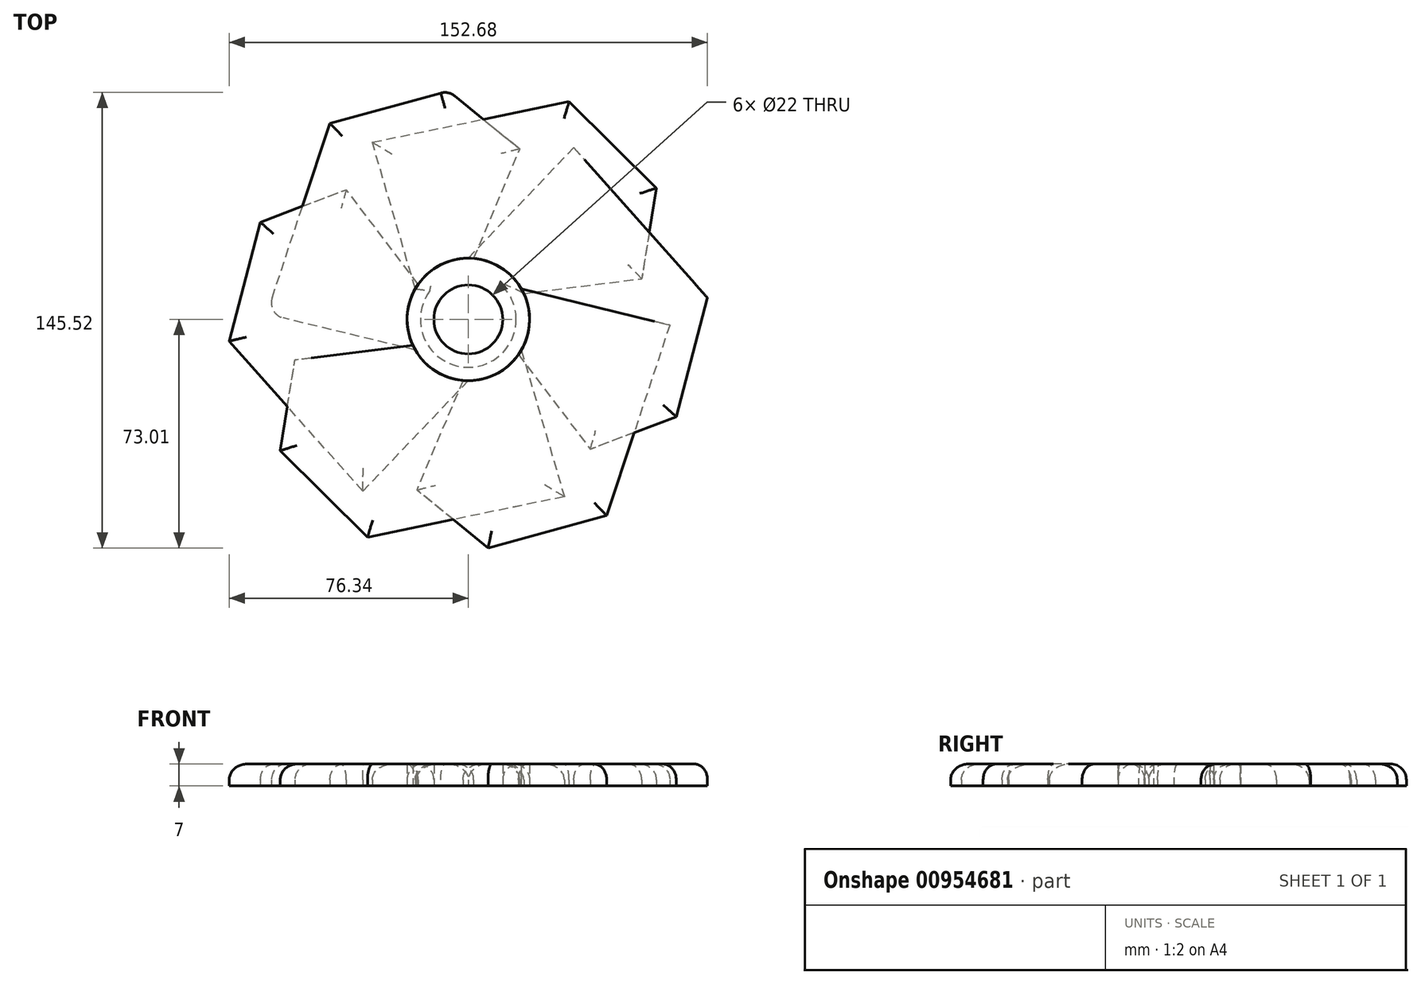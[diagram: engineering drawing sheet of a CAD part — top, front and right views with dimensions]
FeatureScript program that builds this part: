
annotation { "Feature Type Name" : "Feature", "Feature Type Description" : "" }
export const myFeature = defineFeature(function(context is Context, id is Id, definition is map)
    precondition{}
    {
        {
            var Q0;
            Q0=qCreatedBy(makeId("Top.planeOp"),FACE);
            var sketch = newSketch(context, id + "F0", { "sketchPlane" : qUnion([Q0])});
            skArc(sketch, "E0", {"start": v(0, 11) * mm, "mid": v(-7.37, -8.17) * mm, "end": v(10.94, 1.14) * mm});
            skCircle(sketch, "E1", {"center": v(0, 0) * mm, "radius": 11 * mm});
            skArc(sketch, "E2", {"start": v(0, 19.55) * mm, "mid": v(-17.34, -9.03) * mm, "end": v(16.02, -11.21) * mm});
            skArc(sketch, "E3", {"start": v(56.29, -3.64) * mm, "mid": v(30.94, 14.76) * mm, "end": v(0, 19.55) * mm});
            skArc(sketch, "E4", {"start": v(54.87, -7) * mm, "mid": v(34.86, -3.73) * mm, "end": v(16.02, -11.21) * mm});
            skLineSegment(sketch, "E5", {"start": v(56.29, -3.64) * mm, "end": v(56.29, -6.1) * mm});
            skPoint(sketch, "E6.orphan", {"position": v(61.87, -11.21) * mm});
            skPoint(sketch, "E7.visualSharp", {"position": v(56.29, -7.7) * mm});
            skArc(sketch, "E7.filletArc", {"start": v(54.87, -7) * mm, "mid": v(55.82, -6.94) * mm, "end": v(56.29, -6.1) * mm});
            skLineSegment(sketch, "E8", {"start": v(16.02, -11.21) * mm, "end": v(38.94, -41.46) * mm});
            skLineSegment(sketch, "E9", {"start": v(56.29, -7.7) * mm, "end": v(38.94, -41.46) * mm});
            skLineSegment(sketch, "E10", {"start": v(0, 19.55) * mm, "end": v(33.7, 54.86) * mm});
            skLineSegment(sketch, "E11", {"start": v(33.7, 54.86) * mm, "end": v(56.29, -3.64) * mm});
            skLineSegment(sketch, "E12", {"start": v(33.7, 54.86) * mm, "end": v(76.34, 6.93) * mm});
            skLineSegment(sketch, "E13", {"start": v(76.34, 6.93) * mm, "end": v(66.38, -31.05) * mm});
            skLineSegment(sketch, "E14", {"start": v(66.38, -31.05) * mm, "end": v(38.94, -41.46) * mm});
            skSolve(sketch);
        }
        {
            var Q0;
            Q0 = qSketchRegion(id + "F0", true);
            extrude(context, id + "F1", {"entities" : qUnion([Q0]), "endBound" : BoundingType.SYMMETRIC, "depth" : 7 * mm, "offsetDistance" : 25 * mm});
        }
        {
            var Q0;
            Q0=makeQuery(id+"F1.opExtrude","SWEPT_BODY",BODY,{"disambiguationData":[OSD([sQuery(id+"F0.wireOp",EDGE,"E1"),sQuery(id+"F0.wireOp",EDGE,"E2"),sQuery(id+"F0.wireOp",EDGE,"E3"),sQuery(id+"F0.wireOp",EDGE,"E4")])]});
            var Q1;
            Q1=makeQuery(id+"F1.opExtrude","CAP_EDGE",EDGE,{"disambiguationData":[OSD([sQuery(id+"F0.wireOp",EDGE,"E1")])],"isStart":false});
            circularPattern(context, id + "F2", {"entities" : qUnion([Q0]), "axis" : qUnion([Q1]), "angle" : 360 * degree, "instanceCount" : 6, "equalSpace" : true});
        }
        {
            var Q0;
            Q0=makeQuery(id+"F2.opPattern","COPY",EDGE,{"derivedFrom":makeQuery(id+"F1.opExtrude","CAP_EDGE",EDGE,{"disambiguationData":[OSD([sQuery(id+"F0.wireOp",EDGE,"E13")])],"isStart":false}),"instanceName":"2"});
            var Q1;
            Q1=makeQuery(id+"F2.opPattern","COPY",EDGE,{"derivedFrom":makeQuery(id+"F1.opExtrude","CAP_EDGE",EDGE,{"disambiguationData":[OSD([sQuery(id+"F0.wireOp",EDGE,"E12")])],"isStart":false}),"instanceName":"2"});
            fillet(context, id + "F3", {"entities" : qUnion([Q0, Q1]), "tangentPropagation" : true, "radius" : 5 * mm, "defaultsChanged" : false, "vertexSettings" : [], "allowEdgeOverflow" : false});
        }
        {
            var Q0;
            Q0=makeQuery(id+"F2.opPattern","COPY",EDGE,{"derivedFrom":makeQuery(id+"F1.opExtrude","CAP_EDGE",EDGE,{"disambiguationData":[OSD([sQuery(id+"F0.wireOp",EDGE,"E14")])],"isStart":false}),"instanceName":"3"});
            var Q1;
            Q1=makeQuery(id+"F2.opPattern","COPY",EDGE,{"derivedFrom":makeQuery(id+"F1.opExtrude","CAP_EDGE",EDGE,{"disambiguationData":[OSD([sQuery(id+"F0.wireOp",EDGE,"E13")])],"isStart":false}),"instanceName":"3"});
            var Q2;
            Q2=makeQuery(id+"F2.opPattern","COPY",EDGE,{"derivedFrom":makeQuery(id+"F1.opExtrude","CAP_EDGE",EDGE,{"disambiguationData":[OSD([sQuery(id+"F0.wireOp",EDGE,"E12")])],"isStart":false}),"instanceName":"3"});
            var Q3;
            Q3=makeQuery(id+"F2.opPattern","COPY",EDGE,{"derivedFrom":makeQuery(id+"F1.opExtrude","CAP_EDGE",EDGE,{"disambiguationData":[OSD([sQuery(id+"F0.wireOp",EDGE,"E14")])],"isStart":false}),"instanceName":"4"});
            var Q4;
            Q4=makeQuery(id+"F2.opPattern","COPY",EDGE,{"derivedFrom":makeQuery(id+"F1.opExtrude","CAP_EDGE",EDGE,{"disambiguationData":[OSD([sQuery(id+"F0.wireOp",EDGE,"E13")])],"isStart":false}),"instanceName":"4"});
            var Q5;
            Q5=makeQuery(id+"F2.opPattern","COPY",EDGE,{"derivedFrom":makeQuery(id+"F1.opExtrude","CAP_EDGE",EDGE,{"disambiguationData":[OSD([sQuery(id+"F0.wireOp",EDGE,"E12")])],"isStart":false}),"instanceName":"4"});
            var Q6;
            Q6=makeQuery(id+"F2.opPattern","COPY",EDGE,{"derivedFrom":makeQuery(id+"F1.opExtrude","CAP_EDGE",EDGE,{"disambiguationData":[OSD([sQuery(id+"F0.wireOp",EDGE,"E14")])],"isStart":false}),"instanceName":"5"});
            var Q7;
            Q7=makeQuery(id+"F2.opPattern","COPY",EDGE,{"derivedFrom":makeQuery(id+"F1.opExtrude","CAP_EDGE",EDGE,{"disambiguationData":[OSD([sQuery(id+"F0.wireOp",EDGE,"E13")])],"isStart":false}),"instanceName":"5"});
            var Q8;
            Q8=makeQuery(id+"F2.opPattern","COPY",EDGE,{"derivedFrom":makeQuery(id+"F1.opExtrude","CAP_EDGE",EDGE,{"disambiguationData":[OSD([sQuery(id+"F0.wireOp",EDGE,"E12")])],"isStart":false}),"instanceName":"5"});
            var Q9;
            Q9=makeQuery(id+"F1.opExtrude","CAP_EDGE",EDGE,{"disambiguationData":[OSD([sQuery(id+"F0.wireOp",EDGE,"E14")])],"isStart":false});
            var Q10;
            Q10=makeQuery(id+"F1.opExtrude","CAP_EDGE",EDGE,{"disambiguationData":[OSD([sQuery(id+"F0.wireOp",EDGE,"E8")])],"isStart":false});
            var Q11;
            Q11=makeQuery(id+"F2.opPattern","COPY",EDGE,{"derivedFrom":makeQuery(id+"F1.opExtrude","CAP_EDGE",EDGE,{"disambiguationData":[OSD([sQuery(id+"F0.wireOp",EDGE,"E10")])],"isStart":false}),"instanceName":"4"});
            var Q12;
            Q12=makeQuery(id+"F2.opPattern","COPY",EDGE,{"derivedFrom":makeQuery(id+"F1.opExtrude","CAP_EDGE",EDGE,{"disambiguationData":[OSD([sQuery(id+"F0.wireOp",EDGE,"E8")])],"isStart":false}),"instanceName":"5"});
            var Q13;
            Q13=makeQuery(id+"F2.opPattern","COPY",EDGE,{"derivedFrom":makeQuery(id+"F1.opExtrude","CAP_EDGE",EDGE,{"disambiguationData":[OSD([sQuery(id+"F0.wireOp",EDGE,"E10")])],"isStart":false}),"instanceName":"3"});
            var Q14;
            Q14=makeQuery(id+"F2.opPattern","COPY",EDGE,{"derivedFrom":makeQuery(id+"F1.opExtrude","CAP_EDGE",EDGE,{"disambiguationData":[OSD([sQuery(id+"F0.wireOp",EDGE,"E10")])],"isStart":false}),"instanceName":"2"});
            var Q15;
            {var subQ0=sQuery(id+"F0.wireOp",EDGE,"E12");Q15=makeQuery(id+"F3.opFillet","BLEND_EDGE",EDGE,{"blendedFrom":[makeQuery(id+"F2.opPattern","COPY",EDGE,{"derivedFrom":makeQuery(id+"F1.opExtrude","CAP_EDGE",EDGE,{"disambiguationData":[OSD([subQ0])],"isStart":false}),"instanceName":"2"}),makeQuery(id+"F2.opPattern","COPY",FACE,{"derivedFrom":makeQuery(id+"F1.opExtrude","CAP_FACE",FACE,{"disambiguationData":[OSD([sQuery(id+"F0.wireOp",EDGE,"E1"),sQuery(id+"F0.wireOp",EDGE,"E2"),sQuery(id+"F0.wireOp",EDGE,"E8"),sQuery(id+"F0.wireOp",EDGE,"E10"),subQ0,sQuery(id+"F0.wireOp",EDGE,"E13"),sQuery(id+"F0.wireOp",EDGE,"E14")])],"isStart":false}),"instanceName":"2"})],"blendedInto":[makeQuery(id+"F2.opPattern","COPY",FACE,{"derivedFrom":makeQuery(id+"F1.opExtrude","CAP_FACE",FACE,{"disambiguationData":[OSD([sQuery(id+"F0.wireOp",EDGE,"E1"),sQuery(id+"F0.wireOp",EDGE,"E2"),sQuery(id+"F0.wireOp",EDGE,"E8"),sQuery(id+"F0.wireOp",EDGE,"E10"),subQ0,sQuery(id+"F0.wireOp",EDGE,"E13"),sQuery(id+"F0.wireOp",EDGE,"E14")])],"isStart":false}),"instanceName":"2"})]});}
            var Q16;
            Q16=makeQuery(id+"F2.opPattern","COPY",EDGE,{"derivedFrom":makeQuery(id+"F1.opExtrude","CAP_EDGE",EDGE,{"disambiguationData":[OSD([sQuery(id+"F0.wireOp",EDGE,"E8")])],"isStart":false}),"instanceName":"3"});
            var Q17;
            Q17=makeQuery(id+"F2.opPattern","COPY",EDGE,{"derivedFrom":makeQuery(id+"F1.opExtrude","CAP_EDGE",EDGE,{"disambiguationData":[OSD([sQuery(id+"F0.wireOp",EDGE,"E10")])],"isStart":false}),"instanceName":"1"});
            var Q18;
            Q18=makeQuery(id+"F2.opPattern","COPY",FACE,{"derivedFrom":makeQuery(id+"F1.opExtrude","CAP_FACE",FACE,{"disambiguationData":[OSD([sQuery(id+"F0.wireOp",EDGE,"E1"),sQuery(id+"F0.wireOp",EDGE,"E2"),sQuery(id+"F0.wireOp",EDGE,"E8"),sQuery(id+"F0.wireOp",EDGE,"E10"),sQuery(id+"F0.wireOp",EDGE,"E12"),sQuery(id+"F0.wireOp",EDGE,"E13"),sQuery(id+"F0.wireOp",EDGE,"E14")])],"isStart":false}),"instanceName":"1"});
            var Q19;
            Q19=makeQuery(id+"F2.opPattern","COPY",EDGE,{"derivedFrom":makeQuery(id+"F1.opExtrude","CAP_EDGE",EDGE,{"disambiguationData":[OSD([sQuery(id+"F0.wireOp",EDGE,"E14")])],"isStart":false}),"instanceName":"2"});
            var Q20;
            Q20=makeQuery(id+"F2.opPattern","COPY",EDGE,{"derivedFrom":makeQuery(id+"F1.opExtrude","CAP_EDGE",EDGE,{"disambiguationData":[OSD([sQuery(id+"F0.wireOp",EDGE,"E8")])],"isStart":false}),"instanceName":"2"});
            var Q21;
            Q21=makeQuery(id+"F1.opExtrude","CAP_EDGE",EDGE,{"disambiguationData":[OSD([sQuery(id+"F0.wireOp",EDGE,"E10")])],"isStart":false});
            var Q22;
            Q22=makeQuery(id+"F1.opExtrude","CAP_EDGE",EDGE,{"disambiguationData":[OSD([sQuery(id+"F0.wireOp",EDGE,"E13")])],"isStart":false});
            fillet(context, id + "F4", {"entities" : qUnion([Q0, Q1, Q2, Q3, Q4, Q5, Q6, Q7, Q8, Q9, Q10, Q11, Q12, Q13, Q14, Q15, Q16, Q17, Q18, Q19, Q20, Q21, Q22]), "tangentPropagation" : true, "radius" : 5 * mm, "defaultsChanged" : false, "vertexSettings" : [], "allowEdgeOverflow" : false});
        }
    });
